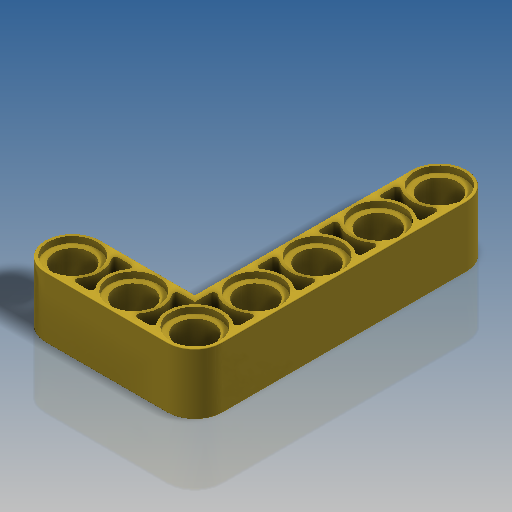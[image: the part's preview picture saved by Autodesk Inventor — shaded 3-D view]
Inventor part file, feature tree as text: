
AUTODESK INVENTOR PART (.ipt)
format: ipt  version: 2018.3 (Build 223284000, 284)  size: 437,760 bytes
history: native  units: mm
features: extrude x3, sketch x2, mirror x1, fillet x1
ambient origin geometry x8: Origin, YZ Plane, XZ Plane, XY Plane, X Axis, Y Axis, Z Axis, Center Point
bodies: Solid1 (feature_tree)
feature tree (7):
  extrude  "Extrusion1"  Depth=6.4mm
  sketch  "Sketch6"  dims[d14=8.0mm d15=0.0mm d32=7.2mm d34=8.0mm d36=0.8mm d41=0.8mm d42=0.0mm d43=3.1mm d44=0.0mm d46=0.4mm d47=0.1mm d49=0.8mm]
  extrude  "Extrusion7"  Depth=7.2mm
  extrude  "Extrusion8"  Depth=8.0mm
  mirror  "Mirror1"
  fillet  "Fillet1"  Radius=0.8mm
  sketch  "Sketch1"  dims[d8=4.8mm d9=6.4mm]
